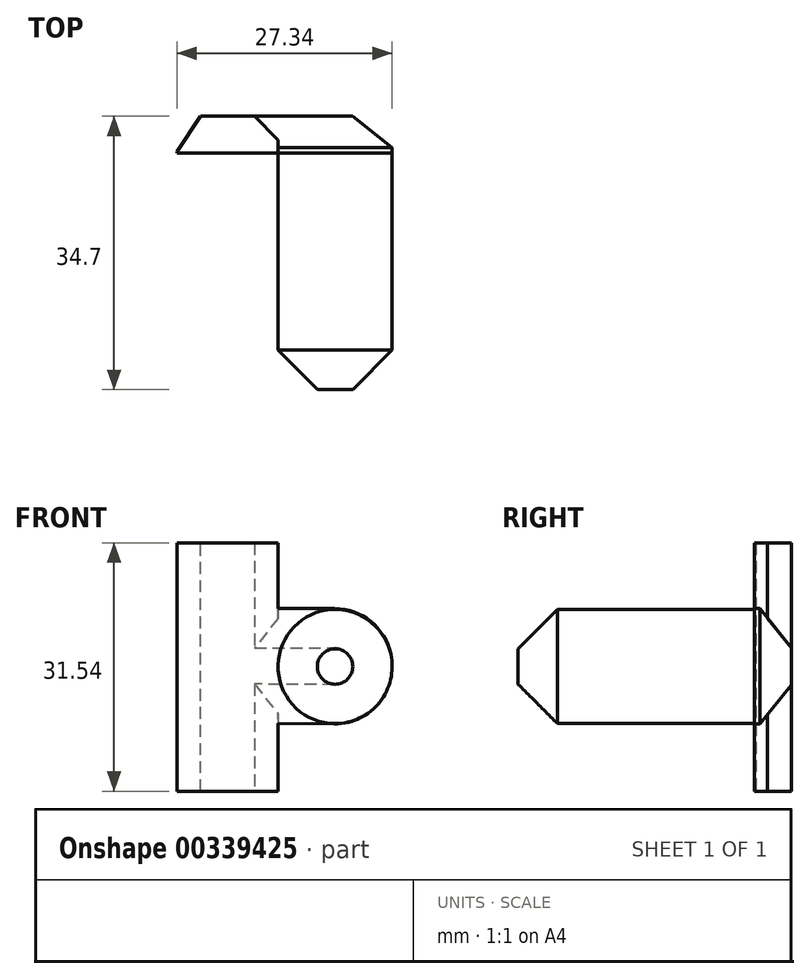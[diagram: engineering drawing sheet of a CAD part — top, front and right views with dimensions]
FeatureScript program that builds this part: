
annotation { "Feature Type Name" : "Feature", "Feature Type Description" : "" }
export const myFeature = defineFeature(function(context is Context, id is Id, definition is map)
    precondition{}
    {
        {
            var Q0;
            Q0=qCreatedBy(makeId("Front.planeOp"),FACE);
            var sketch = newSketch(context, id + "F0", { "sketchPlane" : qUnion([Q0])});
            skCircle(sketch, "E0", {"center": v(0, 0) * mm, "radius": 7.25 * mm});
            skSolve(sketch);
        }
        {
            var Q0;
            Q0=makeQuery(id+"F0.imprint","IMPRINT",FACE,{"disambiguationData":[TD([[makeQuery(id+"F0.imprint","IMPRINT",EDGE,{"derivedFrom":sQuery(id+"F0.wireOp",EDGE,"E0")}),1.0]])]});
            extrude(context, id + "F1", {"entities" : qUnion([Q0]), "depth" : 30 * mm});
        }
        {
            var Q0;
            Q0=makeQuery(id+"F1.opExtrude","CAP_FACE",FACE,{"disambiguationData":[OSD([sQuery(id+"F0.wireOp",EDGE,"E0")])],"isStart":true});
            var sketch = newSketch(context, id + "F2", { "sketchPlane" : qUnion([Q0])});
            skLineSegment(sketch, "E1.bottom", {"start": v(7.23, 7.37) * mm, "end": v(-7.23, 7.37) * mm});
            skLineSegment(sketch, "E1.right", {"start": v(-7.23, 7.37) * mm, "end": v(-7.23, -7.37) * mm});
            skPoint(sketch, "E1.middle", {"position": v(0, 0) * mm});
            skLineSegment(sketch, "E2.0", {"start": v(20.09, 7.16) * mm, "end": v(20.09, -7.16) * mm});
            skLineSegment(sketch, "E3", {"start": v(20.09, 7.16) * mm, "end": v(7.23, 7.37) * mm});
            skPoint(sketch, "E4.start.orphan", {"position": v(7.23, -7.37) * mm});
            skLineSegment(sketch, "E5", {"start": v(-7.23, -7.37) * mm, "end": v(20.09, -7.16) * mm});
            skLineSegment(sketch, "E6", {"start": v(7.23, -15.84) * mm, "end": v(20.09, -15.84) * mm});
            skLineSegment(sketch, "E7", {"start": v(20.09, -15.84) * mm, "end": v(20.09, -7.16) * mm});
            skLineSegment(sketch, "E8", {"start": v(7.23, 7.37) * mm, "end": v(7.23, 15.7) * mm});
            skLineSegment(sketch, "E9", {"start": v(7.23, 15.7) * mm, "end": v(20.09, 15.7) * mm});
            skLineSegment(sketch, "E10", {"start": v(20.09, 15.7) * mm, "end": v(20.09, 7.16) * mm});
            skLineSegment(sketch, "E11", {"start": v(7.23, -15.84) * mm, "end": v(7.23, -7.25) * mm});
            skSolve(sketch);
        }
        {
            var Q0;
            Q0 = qSketchRegion(id + "F2", true);
            extrude(context, id + "F3", {"entities" : qUnion([Q0]), "operationType" : NewBodyOperationType.ADD, "depth" : 4.7 * mm});
        }
        {
            var Q0;
            Q0=makeQuery(id+"F3.opExtrude","SWEPT_EDGE",EDGE,{"disambiguationData":[OSD([sQuery(id+"F2.wireOp",EDGE,"E1.bottom"),sQuery(id+"F2.wireOp",EDGE,"E1.right")])]});
            var Q1;
            Q1=makeQuery(id+"F3.opExtrude","SWEPT_EDGE",EDGE,{"disambiguationData":[OSD([sQuery(id+"F2.wireOp",EDGE,"E1.right"),sQuery(id+"F2.wireOp",EDGE,"E5")])]});
            fillet(context, id + "F4", {"entities" : qUnion([Q0, Q1]), "radius" : 7.3 * mm, "tangentPropagation" : true, "allowEdgeOverflow" : false});
        }
        {
            var Q0;
            {var subQ0=sQuery(id+"F2.wireOp",EDGE,"E1.right");var subQ1=sQuery(id+"F2.wireOp",EDGE,"E1.bottom");Q0=makeQuery(id+"F4.opFillet","BLEND_EDGE",EDGE,{"blendedFrom":[makeQuery(id+"F3.opExtrude","SWEPT_EDGE",EDGE,{"disambiguationData":[OSD([subQ1,subQ0])]}),makeQuery(id+"F3.opExtrude","CAP_FACE",FACE,{"disambiguationData":[OSD([subQ1,subQ0,sQuery(id+"F2.wireOp",EDGE,"E2.0"),sQuery(id+"F2.wireOp",EDGE,"E5"),sQuery(id+"F2.wireOp",EDGE,"E6"),sQuery(id+"F2.wireOp",EDGE,"E7"),sQuery(id+"F2.wireOp",EDGE,"E8"),sQuery(id+"F2.wireOp",EDGE,"E9"),sQuery(id+"F2.wireOp",EDGE,"E10"),sQuery(id+"F2.wireOp",EDGE,"E11")])],"isStart":false})],"blendedInto":[makeQuery(id+"F3.opExtrude","CAP_FACE",FACE,{"disambiguationData":[OSD([subQ1,subQ0,sQuery(id+"F2.wireOp",EDGE,"E2.0"),sQuery(id+"F2.wireOp",EDGE,"E5"),sQuery(id+"F2.wireOp",EDGE,"E6"),sQuery(id+"F2.wireOp",EDGE,"E7"),sQuery(id+"F2.wireOp",EDGE,"E8"),sQuery(id+"F2.wireOp",EDGE,"E9"),sQuery(id+"F2.wireOp",EDGE,"E10"),sQuery(id+"F2.wireOp",EDGE,"E11")])],"isStart":false})]});}
            var Q1;
            {var subQ0=sQuery(id+"F2.wireOp",EDGE,"E5");var subQ1=sQuery(id+"F2.wireOp",EDGE,"E1.right");Q1=makeQuery(id+"F4.opFillet","BLEND_EDGE",EDGE,{"blendedFrom":[makeQuery(id+"F3.opExtrude","SWEPT_EDGE",EDGE,{"disambiguationData":[OSD([subQ1,subQ0])]}),makeQuery(id+"F3.opExtrude","CAP_FACE",FACE,{"disambiguationData":[OSD([sQuery(id+"F2.wireOp",EDGE,"E1.bottom"),subQ1,sQuery(id+"F2.wireOp",EDGE,"E2.0"),subQ0,sQuery(id+"F2.wireOp",EDGE,"E6"),sQuery(id+"F2.wireOp",EDGE,"E7"),sQuery(id+"F2.wireOp",EDGE,"E8"),sQuery(id+"F2.wireOp",EDGE,"E9"),sQuery(id+"F2.wireOp",EDGE,"E10"),sQuery(id+"F2.wireOp",EDGE,"E11")])],"isStart":false})],"blendedInto":[makeQuery(id+"F3.opExtrude","CAP_FACE",FACE,{"disambiguationData":[OSD([sQuery(id+"F2.wireOp",EDGE,"E1.bottom"),subQ1,sQuery(id+"F2.wireOp",EDGE,"E2.0"),subQ0,sQuery(id+"F2.wireOp",EDGE,"E6"),sQuery(id+"F2.wireOp",EDGE,"E7"),sQuery(id+"F2.wireOp",EDGE,"E8"),sQuery(id+"F2.wireOp",EDGE,"E9"),sQuery(id+"F2.wireOp",EDGE,"E10"),sQuery(id+"F2.wireOp",EDGE,"E11")])],"isStart":false})]});}
            chamfer(context, id + "F5", {"entities" : qUnion([Q0, Q1]), "chamferType" : ChamferType.TWO_OFFSETS, "width1" : 5 * mm, "oppositeDirection" : false, "width2" : 4 * mm, "tangentPropagation" : true});
        }
        {
            var Q0;
            Q0=makeQuery(id+"F3.opExtrude","CAP_EDGE",EDGE,{"disambiguationData":[OSD([sQuery(id+"F2.wireOp",EDGE,"E2.0"),sQuery(id+"F2.wireOp",EDGE,"E7"),sQuery(id+"F2.wireOp",EDGE,"E10")])],"isStart":false});
            chamfer(context, id + "F6", {"entities" : qUnion([Q0]), "chamferType" : ChamferType.TWO_OFFSETS, "width1" : 4.5 * mm, "oppositeDirection" : false, "width2" : 3 * mm, "tangentPropagation" : true});
        }
        {
            var Q0;
            Q0=makeQuery(id+"F1.opExtrude","CAP_FACE",FACE,{"disambiguationData":[OSD([sQuery(id+"F0.wireOp",EDGE,"E0")])],"isStart":false});
            chamfer(context, id + "F7", {"entities" : qUnion([Q0]), "width" : 5 * mm, "tangentPropagation" : true});
        }
        {
            var Q0;
            Q0=makeQuery(id+"F3.opExtrude","CAP_EDGE",EDGE,{"disambiguationData":[OSD([sQuery(id+"F2.wireOp",EDGE,"E8")])],"isStart":false});
            var Q1;
            Q1=makeQuery(id+"F3.opExtrude","CAP_EDGE",EDGE,{"disambiguationData":[OSD([sQuery(id+"F2.wireOp",EDGE,"E11")])],"isStart":false});
            chamfer(context, id + "F8", {"entities" : qUnion([Q0, Q1]), "width" : 3 * mm, "tangentPropagation" : true});
        }
    });
